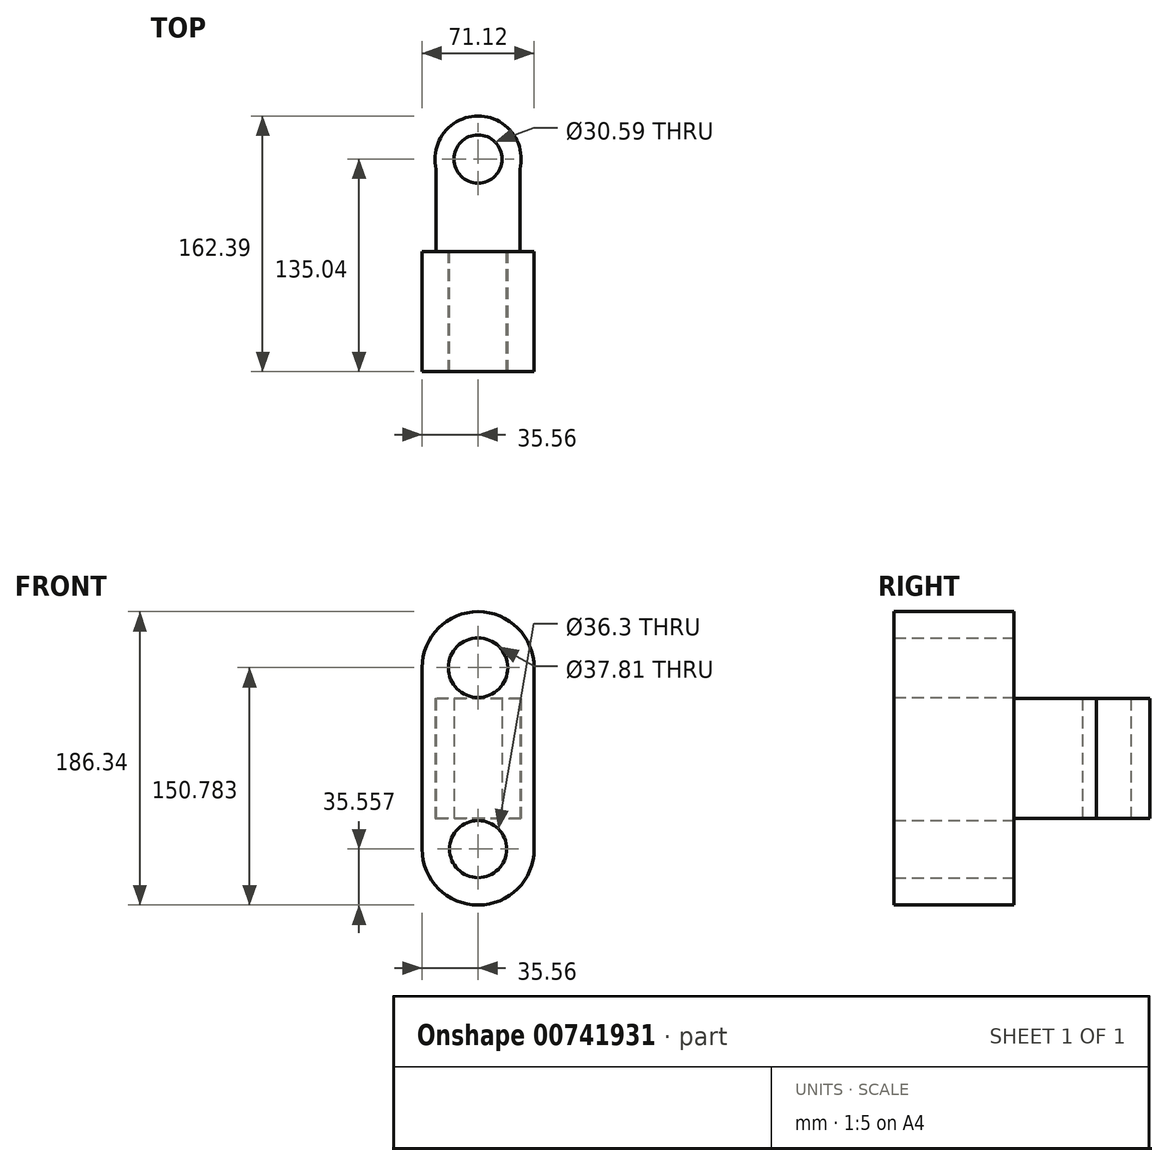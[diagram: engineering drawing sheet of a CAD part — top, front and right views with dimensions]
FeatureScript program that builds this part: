
annotation { "Feature Type Name" : "Feature", "Feature Type Description" : "" }
export const myFeature = defineFeature(function(context is Context, id is Id, definition is map)
    precondition{}
    {
        {
            var Q0;
            Q0=qCreatedBy(makeId("Front.planeOp"),FACE);
            var sketch = newSketch(context, id + "F0", { "sketchPlane" : qUnion([Q0])});
            skLineSegment(sketch, "E0.left", {"start": v(35.56, 57.61) * mm, "end": v(35.56, -57.61) * mm});
            skLineSegment(sketch, "E0.right", {"start": v(-35.56, 57.61) * mm, "end": v(-35.56, -57.61) * mm});
            skPoint(sketch, "E0.middle", {"position": v(0, 0) * mm});
            skArc(sketch, "E1", {"start": v(35.56, 57.61) * mm, "mid": v(0, 93.17) * mm, "end": v(-35.56, 57.61) * mm});
            skArc(sketch, "E2", {"start": v(-35.56, -57.61) * mm, "mid": v(0, -93.17) * mm, "end": v(35.56, -57.61) * mm});
            skCircle(sketch, "E3", {"center": v(0, -57.61) * mm, "radius": 18.15 * mm});
            skCircle(sketch, "E4", {"center": v(0, 57.61) * mm, "radius": 18.9 * mm});
            skSolve(sketch);
        }
        {
            var Q0;
            Q0=makeQuery(id+"F0.imprint","IMPRINT",FACE,{"disambiguationData":[TD([[makeQuery(id+"F0.imprint","IMPRINT",EDGE,{"derivedFrom":sQuery(id+"F0.wireOp",EDGE,"E0.left")}),-1.0]])]});
            extrude(context, id + "F1", {"entities" : qUnion([Q0]), "depth" : 76.2 * mm, "offsetDistance" : 25.4 * mm});
        }
        {
            var Q0;
            Q0=qCreatedBy(makeId("Top.planeOp"),FACE);
            var sketch = newSketch(context, id + "F2", { "sketchPlane" : qUnion([Q0])});
            skLineSegment(sketch, "E5.left", {"start": v(26.57, 58.84) * mm, "end": v(26.57, 0) * mm});
            skLineSegment(sketch, "E5.right", {"start": v(-26.57, 58.84) * mm, "end": v(-26.57, 0) * mm});
            skPoint(sketch, "E5.middle", {"position": v(0, 0) * mm});
            skCircle(sketch, "E6", {"center": v(0, 58.84) * mm, "radius": 15.3 * mm});
            skCircle(sketch, "E7", {"center": v(0, 58.84) * mm, "radius": 27.35 * mm});
            skLineSegment(sketch, "E8", {"start": v(-26.57, 0) * mm, "end": v(26.57, 0) * mm});
            skPoint(sketch, "E9.orphan", {"position": v(-26.57, -58.84) * mm});
            skPoint(sketch, "E10.orphan", {"position": v(26.57, -58.84) * mm});
            skSolve(sketch);
        }
        {
            var Q0;
            Q0=makeQuery(id+"F2.imprint","IMPRINT",FACE,{"disambiguationData":[TD([[makeQuery(id+"F2.imprint","IMPRINT",EDGE,{"derivedFrom":sQuery(id+"F2.wireOp",EDGE,"E6")}),-1.0]])]});
            var Q1;
            {var subQ0=sQuery(id+"F2.wireOp",EDGE,"E8");Q1=makeQuery(id+"F2.imprint","IMPRINT",FACE,{"disambiguationData":[TD([[makeQuery(id+"F2.imprint","IMPRINT",EDGE,{"derivedFrom":subQ0}),1.0]])]});}
            extrude(context, id + "F3", {"entities" : qUnion([Q0, Q1]), "operationType" : NewBodyOperationType.ADD, "depth" : 38.1 * mm, "offsetDistance" : 25.4 * mm, "hasSecondDirection" : true, "secondDirectionOppositeDirection" : true, "secondDirectionDepth" : 38.1 * mm});
        }
    });
